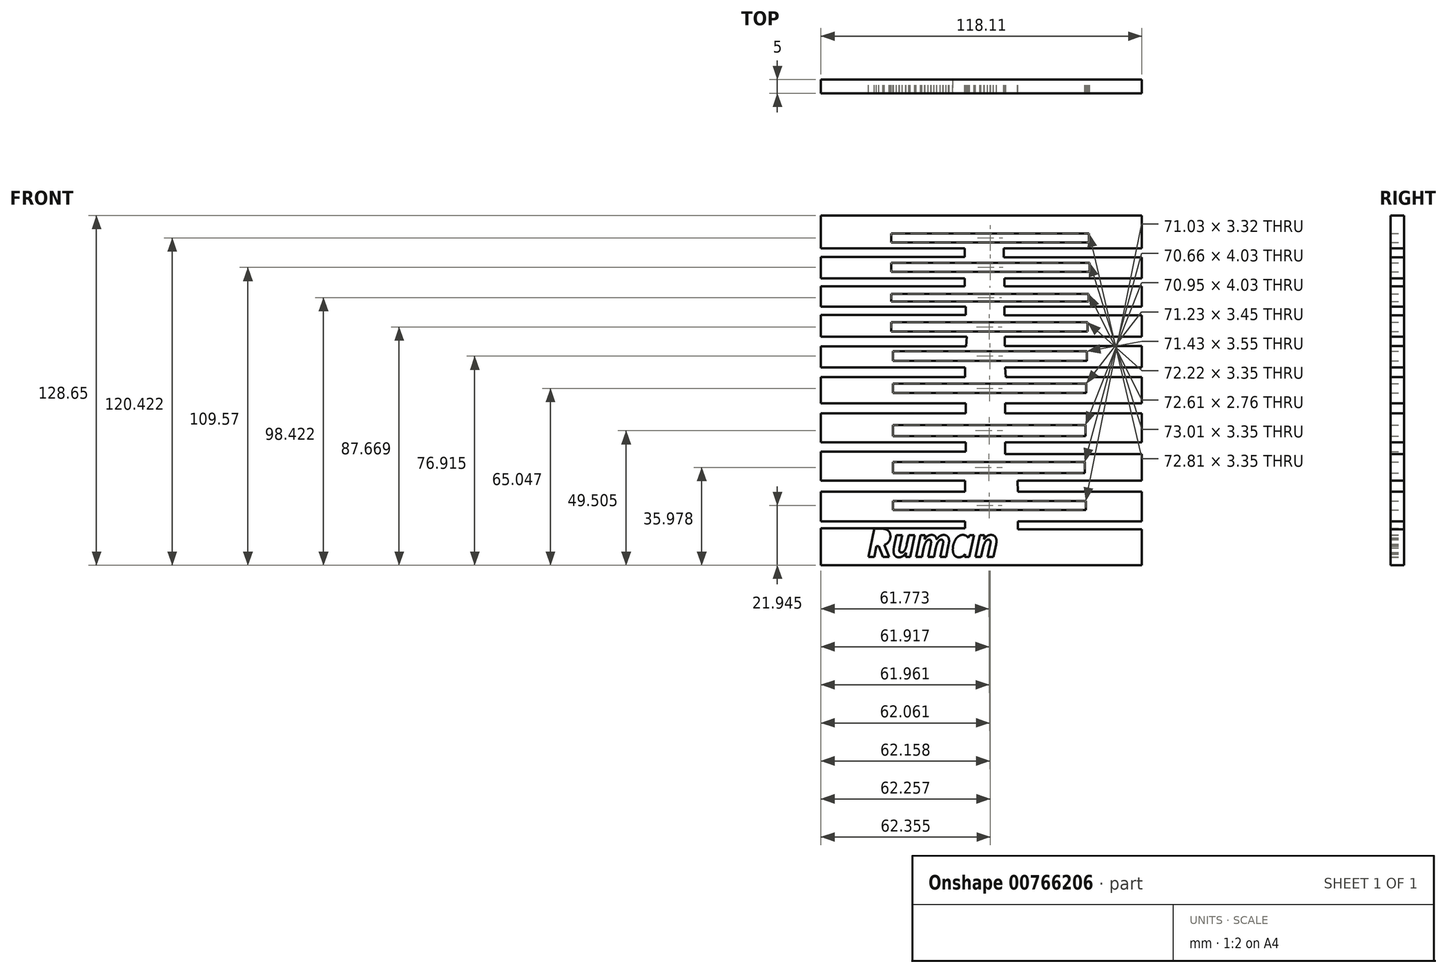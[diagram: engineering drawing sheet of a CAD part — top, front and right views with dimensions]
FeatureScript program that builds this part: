
annotation { "Feature Type Name" : "Feature", "Feature Type Description" : "" }
export const myFeature = defineFeature(function(context is Context, id is Id, definition is map)
    precondition{}
    {
        {
            var Q0;
            Q0=qCreatedBy(makeId("Front.planeOp"),FACE);
            var sketch = newSketch(context, id + "F0", { "sketchPlane" : qUnion([Q0])});
            skLineSegment(sketch, "E0.bottom", {"start": v(-61.27, 59.43) * mm, "end": v(56.84, 59.43) * mm});
            skLineSegment(sketch, "E0.top", {"start": v(-61.27, -69.22) * mm, "end": v(56.84, -69.22) * mm});
            skLineSegment(sketch, "E0.left", {"start": v(-61.27, 59.43) * mm, "end": v(-61.27, 47.35) * mm});
            skLineSegment(sketch, "E0.right", {"start": v(56.84, 59.43) * mm, "end": v(56.84, 47.35) * mm});
            skLineSegment(sketch, "E1.bottom", {"start": v(-34.83, -45.62) * mm, "end": v(36.2, -45.62) * mm});
            skLineSegment(sketch, "E1.top", {"start": v(-34.83, -48.93) * mm, "end": v(36.2, -48.93) * mm});
            skLineSegment(sketch, "E1.left", {"start": v(-34.83, -45.62) * mm, "end": v(-34.83, -48.93) * mm});
            skLineSegment(sketch, "E1.right", {"start": v(36.2, -45.62) * mm, "end": v(36.2, -48.93) * mm});
            skLineSegment(sketch, "E2.bottom", {"start": v(56.84, -38.13) * mm, "end": v(11.08, -38.13) * mm});
            skLineSegment(sketch, "E2.top", {"start": v(56.84, -42.16) * mm, "end": v(11.2, -42.16) * mm});
            skLineSegment(sketch, "E2.right", {"start": v(11.08, -38.13) * mm, "end": v(11.2, -42.16) * mm});
            skLineSegment(sketch, "E3.bottom", {"start": v(-61.27, -38.13) * mm, "end": v(-8.2, -38.13) * mm});
            skLineSegment(sketch, "E3.top", {"start": v(-61.27, -42.16) * mm, "end": v(-8.2, -42.16) * mm});
            skLineSegment(sketch, "E3.right", {"start": v(-8.2, -38.13) * mm, "end": v(-8.2, -42.16) * mm});
            skLineSegment(sketch, "E4.trimOffspring", {"start": v(-61.27, -42.16) * mm, "end": v(-61.27, -53.08) * mm});
            skLineSegment(sketch, "E5.trimOffspring", {"start": v(56.84, -42.16) * mm, "end": v(56.84, -53.08) * mm});
            skLineSegment(sketch, "E6.bottom", {"start": v(-34.83, -31.23) * mm, "end": v(35.83, -31.23) * mm});
            skLineSegment(sketch, "E6.top", {"start": v(-34.83, -35.26) * mm, "end": v(35.83, -35.26) * mm});
            skLineSegment(sketch, "E6.left", {"start": v(-34.83, -31.23) * mm, "end": v(-34.83, -35.26) * mm});
            skLineSegment(sketch, "E6.right", {"start": v(35.83, -31.23) * mm, "end": v(35.83, -35.26) * mm});
            skLineSegment(sketch, "E7.bottom", {"start": v(56.84, -24.03) * mm, "end": v(6.48, -24.03) * mm});
            skLineSegment(sketch, "E7.top", {"start": v(56.84, -28.35) * mm, "end": v(6.48, -28.35) * mm});
            skLineSegment(sketch, "E7.right", {"start": v(6.48, -24.03) * mm, "end": v(6.48, -28.35) * mm});
            skLineSegment(sketch, "E8.bottom", {"start": v(-61.27, -24.03) * mm, "end": v(-7.91, -24.03) * mm});
            skLineSegment(sketch, "E8.top", {"start": v(-61.27, -27.49) * mm, "end": v(-7.91, -27.49) * mm});
            skLineSegment(sketch, "E8.right", {"start": v(-7.91, -24.03) * mm, "end": v(-7.91, -27.49) * mm});
            skLineSegment(sketch, "E9.bottom", {"start": v(-34.83, -17.7) * mm, "end": v(36.12, -17.7) * mm});
            skLineSegment(sketch, "E9.top", {"start": v(-34.83, -21.73) * mm, "end": v(36.12, -21.73) * mm});
            skLineSegment(sketch, "E9.left", {"start": v(-34.83, -17.7) * mm, "end": v(-34.83, -21.73) * mm});
            skLineSegment(sketch, "E9.right", {"start": v(36.12, -17.7) * mm, "end": v(36.12, -21.73) * mm});
            skLineSegment(sketch, "E10.bottom", {"start": v(-7.91, -9.64) * mm, "end": v(-61.27, -9.64) * mm});
            skLineSegment(sketch, "E10.top", {"start": v(-7.91, -13.38) * mm, "end": v(-61.27, -13.38) * mm});
            skLineSegment(sketch, "E10.left", {"start": v(-7.91, -9.64) * mm, "end": v(-7.91, -13.38) * mm});
            skLineSegment(sketch, "E11.bottom", {"start": v(6.48, -9.64) * mm, "end": v(56.84, -9.64) * mm});
            skLineSegment(sketch, "E11.top", {"start": v(6.48, -13.38) * mm, "end": v(56.84, -13.38) * mm});
            skLineSegment(sketch, "E11.left", {"start": v(6.48, -9.64) * mm, "end": v(6.48, -13.38) * mm});
            skLineSegment(sketch, "E12.trimOffspring", {"start": v(-61.27, -13.38) * mm, "end": v(-61.27, -24.03) * mm});
            skLineSegment(sketch, "E13.trimOffspring", {"start": v(56.84, -13.38) * mm, "end": v(56.84, -24.03) * mm});
            skLineSegment(sketch, "E14.bottom", {"start": v(-34.83, -2.45) * mm, "end": v(36.4, -2.45) * mm});
            skLineSegment(sketch, "E14.top", {"start": v(-34.83, -5.9) * mm, "end": v(36.4, -5.9) * mm});
            skLineSegment(sketch, "E14.left", {"start": v(-34.83, -2.45) * mm, "end": v(-34.83, -5.9) * mm});
            skLineSegment(sketch, "E14.right", {"start": v(36.4, -2.45) * mm, "end": v(36.4, -5.9) * mm});
            skLineSegment(sketch, "E15.bottom", {"start": v(-61.27, 3.6) * mm, "end": v(-8.2, 3.6) * mm});
            skLineSegment(sketch, "E15.top", {"start": v(-61.27, 0) * mm, "end": v(-8.2, 0) * mm});
            skLineSegment(sketch, "E15.right", {"start": v(-8.2, 3.6) * mm, "end": v(-8.2, 0) * mm});
            skLineSegment(sketch, "E16.trimOffspring", {"start": v(-61.27, 0) * mm, "end": v(-61.27, -9.64) * mm});
            skLineSegment(sketch, "E17.bottom", {"start": v(56.84, 3.6) * mm, "end": v(6.48, 3.6) * mm});
            skLineSegment(sketch, "E17.top", {"start": v(56.84, 0) * mm, "end": v(6.76, 0) * mm});
            skLineSegment(sketch, "E17.right", {"start": v(6.48, 3.6) * mm, "end": v(6.76, 0) * mm});
            skLineSegment(sketch, "E18.trimOffspring", {"start": v(56.84, 0) * mm, "end": v(56.84, -9.64) * mm});
            skLineSegment(sketch, "E19.trimOffspring", {"start": v(56.84, -28.35) * mm, "end": v(56.84, -38.13) * mm});
            skLineSegment(sketch, "E20.trimOffspring", {"start": v(-61.27, -27.49) * mm, "end": v(-61.27, -38.13) * mm});
            skLineSegment(sketch, "E21.bottom", {"start": v(-34.83, 9.47) * mm, "end": v(36.6, 9.47) * mm});
            skLineSegment(sketch, "E21.top", {"start": v(-34.83, 5.92) * mm, "end": v(36.6, 5.92) * mm});
            skLineSegment(sketch, "E21.left", {"start": v(-34.83, 9.47) * mm, "end": v(-34.83, 5.92) * mm});
            skLineSegment(sketch, "E21.right", {"start": v(36.6, 9.47) * mm, "end": v(36.6, 5.92) * mm});
            skLineSegment(sketch, "E22.bottom", {"start": v(-61.27, 14.8) * mm, "end": v(-7.6, 14.8) * mm});
            skLineSegment(sketch, "E22.top", {"start": v(-61.27, 11.25) * mm, "end": v(-7.8, 11.25) * mm});
            skLineSegment(sketch, "E22.right", {"start": v(-7.6, 14.8) * mm, "end": v(-7.8, 11.25) * mm});
            skLineSegment(sketch, "E23.trimOffspring", {"start": v(-61.27, 11.25) * mm, "end": v(-61.27, 3.6) * mm});
            skLineSegment(sketch, "E24.bottom", {"start": v(56.84, 14.8) * mm, "end": v(6.41, 14.8) * mm});
            skLineSegment(sketch, "E24.top", {"start": v(56.84, 11.44) * mm, "end": v(6.41, 11.44) * mm});
            skLineSegment(sketch, "E24.right", {"start": v(6.41, 14.8) * mm, "end": v(6.41, 11.44) * mm});
            skLineSegment(sketch, "E25.trimOffspring", {"start": v(56.84, 11.44) * mm, "end": v(56.84, 3.6) * mm});
            skLineSegment(sketch, "E26.bottom", {"start": v(-35.42, 20.13) * mm, "end": v(36.8, 20.13) * mm});
            skLineSegment(sketch, "E26.top", {"start": v(-35.42, 16.77) * mm, "end": v(36.8, 16.77) * mm});
            skLineSegment(sketch, "E26.left", {"start": v(-35.42, 20.13) * mm, "end": v(-35.42, 16.77) * mm});
            skLineSegment(sketch, "E26.right", {"start": v(36.8, 20.13) * mm, "end": v(36.8, 16.77) * mm});
            skLineSegment(sketch, "E27.bottom", {"start": v(-61.27, 25.85) * mm, "end": v(-8, 25.85) * mm});
            skLineSegment(sketch, "E27.top", {"start": v(-61.27, 22.89) * mm, "end": v(-8, 22.89) * mm});
            skLineSegment(sketch, "E27.right", {"start": v(-8, 25.85) * mm, "end": v(-8, 22.89) * mm});
            skLineSegment(sketch, "E28.trimOffspring", {"start": v(-61.27, 22.89) * mm, "end": v(-61.27, 14.8) * mm});
            skLineSegment(sketch, "E29.bottom", {"start": v(56.84, 25.85) * mm, "end": v(6.22, 25.85) * mm});
            skLineSegment(sketch, "E29.top", {"start": v(56.84, 22.7) * mm, "end": v(6.22, 22.7) * mm});
            skLineSegment(sketch, "E29.right", {"start": v(6.22, 25.85) * mm, "end": v(6.22, 22.7) * mm});
            skLineSegment(sketch, "E30.trimOffspring", {"start": v(56.84, 22.7) * mm, "end": v(56.84, 14.8) * mm});
            skLineSegment(sketch, "E31.bottom", {"start": v(-35.42, 30.58) * mm, "end": v(37.2, 30.58) * mm});
            skLineSegment(sketch, "E31.top", {"start": v(-35.42, 27.82) * mm, "end": v(37.2, 27.82) * mm});
            skLineSegment(sketch, "E31.left", {"start": v(-35.42, 30.58) * mm, "end": v(-35.42, 27.82) * mm});
            skLineSegment(sketch, "E31.right", {"start": v(37.2, 30.58) * mm, "end": v(37.2, 27.82) * mm});
            skLineSegment(sketch, "E32.bottom", {"start": v(-61.27, 36.3) * mm, "end": v(-8.39, 36.3) * mm});
            skLineSegment(sketch, "E32.top", {"start": v(-61.27, 33.35) * mm, "end": v(-8.39, 33.35) * mm});
            skLineSegment(sketch, "E32.right", {"start": v(-8.39, 36.3) * mm, "end": v(-8.39, 33.35) * mm});
            skLineSegment(sketch, "E33.trimOffspring", {"start": v(-61.27, 33.35) * mm, "end": v(-61.27, 25.85) * mm});
            skLineSegment(sketch, "E34.bottom", {"start": v(56.84, 36.3) * mm, "end": v(6.22, 36.3) * mm});
            skLineSegment(sketch, "E34.top", {"start": v(56.84, 33.35) * mm, "end": v(6.22, 33.35) * mm});
            skLineSegment(sketch, "E34.right", {"start": v(6.22, 36.3) * mm, "end": v(6.22, 33.35) * mm});
            skLineSegment(sketch, "E35.trimOffspring", {"start": v(56.84, 33.35) * mm, "end": v(56.84, 25.85) * mm});
            skLineSegment(sketch, "E36.bottom", {"start": v(-35.42, 42.03) * mm, "end": v(37.59, 42.03) * mm});
            skLineSegment(sketch, "E36.top", {"start": v(-35.42, 38.67) * mm, "end": v(37.59, 38.67) * mm});
            skLineSegment(sketch, "E36.left", {"start": v(-35.42, 42.03) * mm, "end": v(-35.42, 38.67) * mm});
            skLineSegment(sketch, "E36.right", {"start": v(37.59, 42.03) * mm, "end": v(37.59, 38.67) * mm});
            skLineSegment(sketch, "E37.bottom", {"start": v(-61.27, 47.35) * mm, "end": v(-8.39, 47.35) * mm});
            skLineSegment(sketch, "E37.top", {"start": v(-61.27, 44.2) * mm, "end": v(-8.39, 44.2) * mm});
            skLineSegment(sketch, "E37.right", {"start": v(-8.39, 47.35) * mm, "end": v(-8.39, 44.2) * mm});
            skLineSegment(sketch, "E38.trimOffspring", {"start": v(-61.27, 44.2) * mm, "end": v(-61.27, 36.3) * mm});
            skLineSegment(sketch, "E39.bottom", {"start": v(56.84, 47.35) * mm, "end": v(6.02, 47.35) * mm});
            skLineSegment(sketch, "E39.top", {"start": v(56.84, 44) * mm, "end": v(6.02, 44) * mm});
            skLineSegment(sketch, "E39.right", {"start": v(6.02, 47.35) * mm, "end": v(6.02, 44) * mm});
            skLineSegment(sketch, "E40.trimOffspring", {"start": v(56.84, 44) * mm, "end": v(56.84, 36.3) * mm});
            skLineSegment(sketch, "E41.bottom", {"start": v(-35.42, 52.88) * mm, "end": v(37.4, 52.88) * mm});
            skLineSegment(sketch, "E41.top", {"start": v(-35.42, 49.53) * mm, "end": v(37.4, 49.53) * mm});
            skLineSegment(sketch, "E41.left", {"start": v(-35.42, 52.88) * mm, "end": v(-35.42, 49.53) * mm});
            skLineSegment(sketch, "E41.right", {"start": v(37.4, 52.88) * mm, "end": v(37.4, 49.53) * mm});
            skLineSegment(sketch, "E42.bottom", {"start": v(-8.2, -53.08) * mm, "end": v(-61.27, -53.08) * mm});
            skLineSegment(sketch, "E42.top", {"start": v(-8.2, -55.7) * mm, "end": v(-61.27, -55.7) * mm});
            skLineSegment(sketch, "E42.left", {"start": v(-8.2, -53.08) * mm, "end": v(-8.2, -55.7) * mm});
            skLineSegment(sketch, "E43.bottom", {"start": v(56.84, -53.08) * mm, "end": v(11.2, -53.08) * mm});
            skLineSegment(sketch, "E43.top", {"start": v(56.84, -56.04) * mm, "end": v(11.2, -56.04) * mm});
            skLineSegment(sketch, "E43.right", {"start": v(11.2, -53.08) * mm, "end": v(11.2, -56.04) * mm});
            skLineSegment(sketch, "E44.trimOffspring", {"start": v(-61.27, -55.7) * mm, "end": v(-61.27, -69.22) * mm});
            skLineSegment(sketch, "E45.trimOffspring", {"start": v(56.84, -56.04) * mm, "end": v(56.84, -69.22) * mm});
            skText(sketch, "E46", { "text": "Ruman", "fontName": "OpenSans-BoldItalic.ttf"});
            const initialGuessF0  = {"E46": [-0.0442, -0.06617, 1, 0, 0.01048]};
            skSetInitialGuess(sketch, initialGuessF0);
            skSolve(sketch);
        }
        {
            var Q0;
            Q0=makeQuery(id+"F0.imprint","IMPRINT",FACE,{"disambiguationData":[TD([[makeQuery(id+"F0.imprint","IMPRINT",EDGE,{"derivedFrom":sQuery(id+"F0.wireOp",EDGE,"E0.bottom")}),-1.0]])]});
            extrude(context, id + "F1", {"entities" : qUnion([Q0]), "depth" : 5 * mm, "offsetDistance" : 25.4 * mm});
        }
    });
